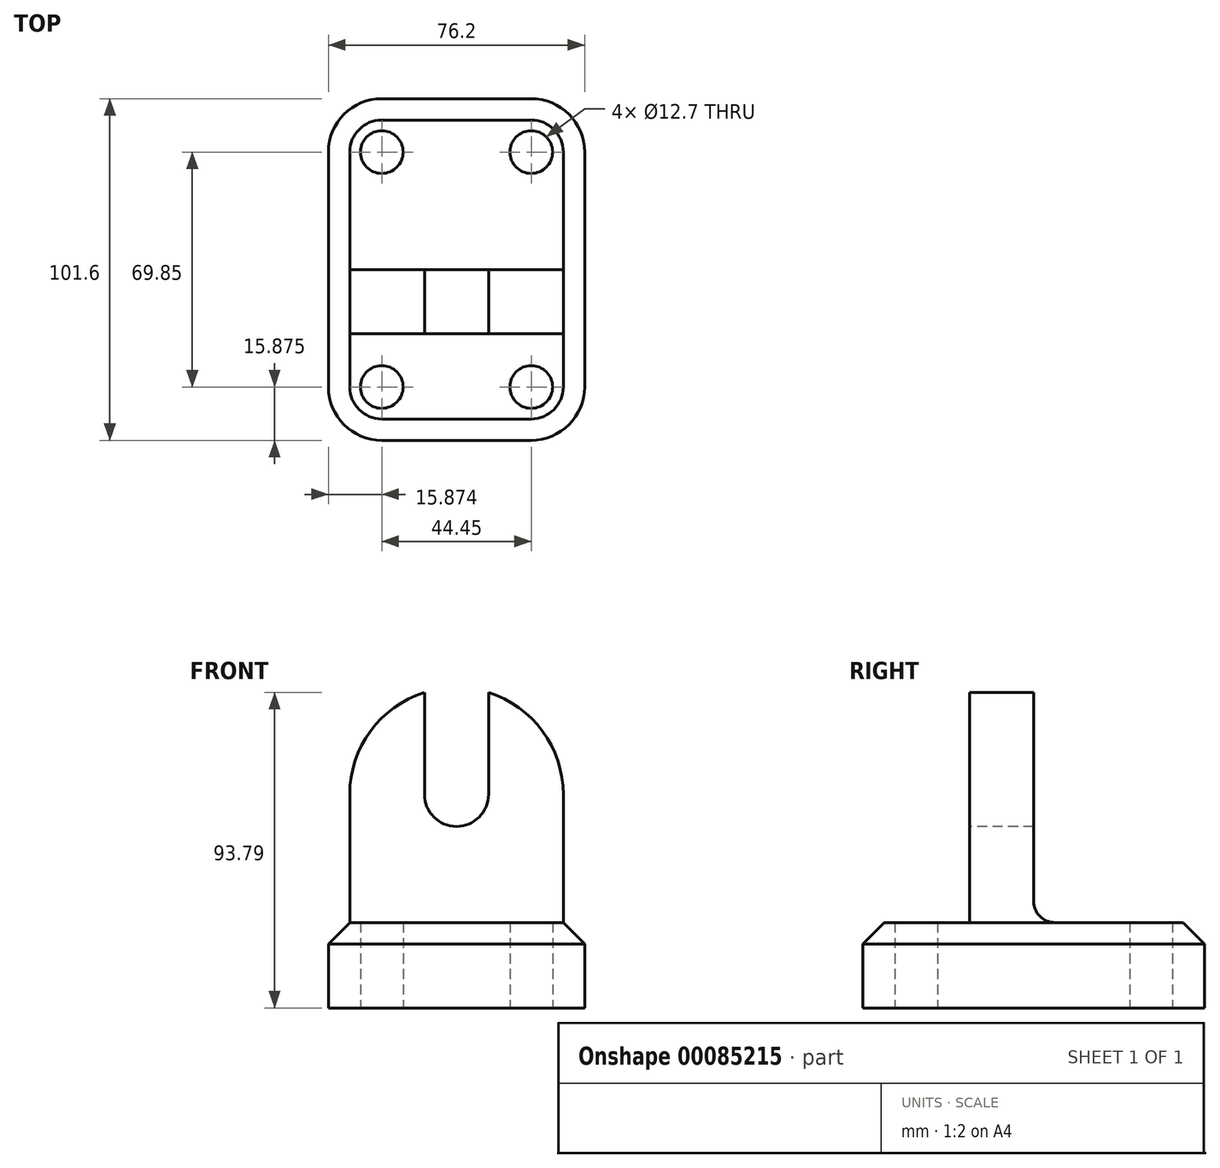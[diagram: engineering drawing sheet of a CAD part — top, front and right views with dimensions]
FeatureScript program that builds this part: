
annotation { "Feature Type Name" : "Feature", "Feature Type Description" : "" }
export const myFeature = defineFeature(function(context is Context, id is Id, definition is map)
    precondition{}
    {
        {
            var Q0;
            Q0=qCreatedBy(makeId("Top.planeOp"),FACE);
            var sketch = newSketch(context, id + "F0", { "sketchPlane" : qUnion([Q0])});
            skLineSegment(sketch, "E0.bottom", {"start": v(-23.1, 42) * mm, "end": v(21.34, 42) * mm});
            skLineSegment(sketch, "E0.top", {"start": v(-23.1, -59.6) * mm, "end": v(21.34, -59.6) * mm});
            skLineSegment(sketch, "E0.left", {"start": v(-38.98, 26.13) * mm, "end": v(-38.98, -43.72) * mm});
            skLineSegment(sketch, "E0.right", {"start": v(37.22, 26.13) * mm, "end": v(37.22, -43.72) * mm});
            skPoint(sketch, "E1.visualSharp", {"position": v(-38.98, 42) * mm});
            skArc(sketch, "E1.filletArc", {"start": v(-23.1, 42) * mm, "mid": v(-34.33, 37.35) * mm, "end": v(-38.98, 26.13) * mm});
            skPoint(sketch, "E2.visualSharp", {"position": v(37.22, 42) * mm});
            skArc(sketch, "E2.filletArc", {"start": v(37.22, 26.13) * mm, "mid": v(32.57, 37.35) * mm, "end": v(21.34, 42) * mm});
            skPoint(sketch, "E3.visualSharp", {"position": v(37.22, -59.6) * mm});
            skArc(sketch, "E3.filletArc", {"start": v(21.34, -59.6) * mm, "mid": v(32.57, -54.95) * mm, "end": v(37.22, -43.72) * mm});
            skPoint(sketch, "E4.visualSharp", {"position": v(-38.98, -59.6) * mm});
            skArc(sketch, "E4.filletArc", {"start": v(-38.98, -43.72) * mm, "mid": v(-34.33, -54.95) * mm, "end": v(-23.1, -59.6) * mm});
            skSolve(sketch);
        }
        {
            var Q0;
            Q0=makeQuery(id+"F0.imprint","IMPRINT",FACE,{"disambiguationData":[TD([[makeQuery(id+"F0.imprint","IMPRINT",EDGE,{"derivedFrom":sQuery(id+"F0.wireOp",EDGE,"E0.bottom")}),-1.0]])]});
            extrude(context, id + "F1", {"entities" : qUnion([Q0]), "depth" : 25.4 * mm});
        }
        {
            var Q0;
            Q0=makeQuery(id+"F1.opExtrude","CAP_EDGE",EDGE,{"disambiguationData":[OSD([sQuery(id+"F0.wireOp",EDGE,"E0.bottom")])],"isStart":false});
            chamfer(context, id + "F2", {"entities" : qUnion([Q0]), "width" : 6.35 * mm, "tangentPropagation" : true});
        }
        {
            var Q0;
            Q0=makeQuery(id+"F1.opExtrude","CAP_FACE",FACE,{"disambiguationData":[OSD([sQuery(id+"F0.wireOp",EDGE,"E0.bottom"),sQuery(id+"F0.wireOp",EDGE,"E0.top"),sQuery(id+"F0.wireOp",EDGE,"E0.left"),sQuery(id+"F0.wireOp",EDGE,"E0.right"),sQuery(id+"F0.wireOp",EDGE,"E1.filletArc"),sQuery(id+"F0.wireOp",EDGE,"E2.filletArc"),sQuery(id+"F0.wireOp",EDGE,"E3.filletArc"),sQuery(id+"F0.wireOp",EDGE,"E4.filletArc")])],"isStart":false});
            var sketch = newSketch(context, id + "F3", { "sketchPlane" : qUnion([Q0])});
            skLineSegment(sketch, "E5.bottom", {"start": v(-32.63, -8.8) * mm, "end": v(30.87, -8.8) * mm});
            skLineSegment(sketch, "E5.top", {"start": v(-32.63, -27.85) * mm, "end": v(30.87, -27.85) * mm});
            skLineSegment(sketch, "E5.left", {"start": v(-32.63, -8.8) * mm, "end": v(-32.63, -27.85) * mm});
            skLineSegment(sketch, "E5.right", {"start": v(30.87, -8.8) * mm, "end": v(30.87, -27.85) * mm});
            skSolve(sketch);
        }
        {
            var Q0;
            Q0 = qSketchRegion(id + "F3", true);
            extrude(context, id + "F4", {"entities" : qUnion([Q0]), "operationType" : NewBodyOperationType.ADD, "depth" : 95.25 * mm});
        }
        {
            var Q0;
            Q0=makeQuery(id+"F4.opExtrude","SWEPT_FACE",FACE,{"disambiguationData":[OSD([sQuery(id+"F3.wireOp",EDGE,"E5.top")])]});
            var sketch = newSketch(context, id + "F5", { "sketchPlane" : qUnion([Q0])});
            skPoint(sketch, "E6", {"position": v(-0.88, 63.5) * mm});
            skArc(sketch, "E7", {"start": v(30.87, 63.5) * mm, "mid": v(-0.88, 95.25) * mm, "end": v(-32.63, 63.5) * mm});
            skCircle(sketch, "E8", {"center": v(-0.88, 63.5) * mm, "radius": 9.53 * mm});
            skLineSegment(sketch, "E9", {"start": v(8.64, 25.4) * mm, "end": v(8.64, 93.79) * mm});
            skLineSegment(sketch, "E10", {"start": v(-10.4, 93.79) * mm, "end": v(-10.4, 25.4) * mm});
            skSolve(sketch);
        }
        {
            var Q0;
            {var subQ0=sQuery(id+"F5.wireOp",EDGE,"E7");var subQ1=sQuery(id+"F3.wireOp",EDGE,"E5.top");var subQ4=makeQuery(id+"F4.opExtrude","CAP_EDGE",EDGE,{"disambiguationData":[OSD([subQ1])],"isStart":false});var subQ5=makeQuery(id+"F5.imprint","INTERSECT",VERTEX,{"derivedFrom":[subQ4,subQ0]});Q0=makeQuery(id+"F5.imprint","IMPRINT",FACE,{"disambiguationData":[TD([[makeQuery(id+"F5.imprint","IMPRINT",EDGE,{"disambiguationData":[TD([[subQ5,-1.0]])],"derivedFrom":subQ0}),-1.0]])]});}
            var Q1;
            {var subQ0=sQuery(id+"F5.wireOp",EDGE,"E7");var subQ1=sQuery(id+"F3.wireOp",EDGE,"E5.top");var subQ4=makeQuery(id+"F4.opExtrude","CAP_EDGE",EDGE,{"disambiguationData":[OSD([subQ1])],"isStart":false});var subQ5=makeQuery(id+"F5.imprint","INTERSECT",VERTEX,{"derivedFrom":[subQ4,subQ0]});Q1=makeQuery(id+"F5.imprint","IMPRINT",FACE,{"disambiguationData":[TD([[makeQuery(id+"F5.imprint","IMPRINT",EDGE,{"disambiguationData":[TD([[subQ5,1.0]])],"derivedFrom":subQ0}),-1.0]])]});}
            extrude(context, id + "F6", {"entities" : qUnion([Q0, Q1]), "operationType" : NewBodyOperationType.REMOVE, "oppositeDirection" : true, "depth" : 25.4 * mm});
        }
        {
            var Q0;
            {var subQ0=sQuery(id+"F5.wireOp",EDGE,"E8");var subQ1=makeQuery(id+"F5.imprint","INTERSECT",VERTEX,{"derivedFrom":[subQ0,sQuery(id+"F5.wireOp",EDGE,"E9")]});Q0=makeQuery(id+"F5.imprint","IMPRINT",FACE,{"disambiguationData":[TD([[makeQuery(id+"F5.imprint","IMPRINT",EDGE,{"disambiguationData":[TD([[subQ1,-1.0]])],"derivedFrom":subQ0}),1.0]])]});}
            var Q1;
            {var subQ0=sQuery(id+"F5.wireOp",EDGE,"E9");var subQ1=sQuery(id+"F5.wireOp",EDGE,"E7");var subQ2=makeQuery(id+"F5.imprint","INTERSECT",VERTEX,{"derivedFrom":[subQ1,subQ0]});Q1=makeQuery(id+"F5.imprint","IMPRINT",FACE,{"disambiguationData":[TD([[makeQuery(id+"F5.imprint","IMPRINT",EDGE,{"disambiguationData":[TD([[subQ2,-1.0]])],"derivedFrom":subQ1}),1.0]])]});}
            extrude(context, id + "F7", {"entities" : qUnion([Q0, Q1]), "operationType" : NewBodyOperationType.REMOVE, "oppositeDirection" : true, "depth" : 25.4 * mm});
        }
        {
            var Q0;
            Q0=sQuery(id+"F0.wireOp",VERTEX,"E4.filletArc.center");
            var Q1;
            Q1=sQuery(id+"F0.wireOp",VERTEX,"E3.filletArc.center");
            var Q2;
            Q2=sQuery(id+"F0.wireOp",VERTEX,"E1.filletArc.center");
            var Q3;
            Q3=sQuery(id+"F0.wireOp",VERTEX,"E2.filletArc.center");
            var Q4;
            Q4=makeQuery(id+"F1.opExtrude","SWEPT_BODY",BODY,{"disambiguationData":[OSD([sQuery(id+"F0.wireOp",EDGE,"E0.bottom"),sQuery(id+"F0.wireOp",EDGE,"E0.top"),sQuery(id+"F0.wireOp",EDGE,"E0.left"),sQuery(id+"F0.wireOp",EDGE,"E0.right"),sQuery(id+"F0.wireOp",EDGE,"E1.filletArc"),sQuery(id+"F0.wireOp",EDGE,"E2.filletArc"),sQuery(id+"F0.wireOp",EDGE,"E3.filletArc"),sQuery(id+"F0.wireOp",EDGE,"E4.filletArc")])]});
            hole(context, id + "F8", {"style" : HoleStyle.SIMPLE, "endStyle" : HoleEndStyle.THROUGH, "oppositeDirection" : true, "holeDiameter" : 12.7 * mm, "locations" : qUnion([Q0, Q1, Q2, Q3]), "scope" : qUnion([Q4]), "isTappedThrough" : true});
        }
        {
            var Q0;
            Q0=makeQuery(id+"F4.opExtrude","CAP_EDGE",EDGE,{"disambiguationData":[OSD([sQuery(id+"F3.wireOp",EDGE,"E5.bottom")])],"isStart":true});
            var Q1;
            Q1=makeQuery(id+"F4.opExtrude","CAP_EDGE",EDGE,{"disambiguationData":[OSD([sQuery(id+"F3.wireOp",EDGE,"E5.top")])],"isStart":true});
            fillet(context, id + "F9", {"entities" : qUnion([Q0, Q1]), "radius" : 6.35 * mm, "tangentPropagation" : true, "allowEdgeOverflow" : false});
        }
    });
